# Revit family: Hand Dryer_Metlam_ABS
name_source: partatom
category: Specialty Equipment
revit_build: Autodesk Revit 2016 (Build: 20170117_1200(x64)
units: mm (PartAtom-declared; Revit-internal decimal feet)

## family parameters
Always vertical = Yes
Cut with Voids When Loaded = No
OmniClass Number = 23.40.20.21.14
OmniClass Title = Hand and Hair Dryers
Part Type = Normal
Room Calculation Point = Yes
Round Connector Dimension = Use Diameter
Shared = No
Work Plane-Based = No

## types (1)
- 260w x 180d x 217h (ML_1800_WHT)
    Description = Auto Operation ABS Hand Dryer
    Manufacturer = Metlam
    Manufacturer_Overall Depth = 180 mm  [stored 0.590551 ft]
    Manufacturer_Overall Height = 217 mm  [stored 0.711942 ft]
    Manufacturer_Overall Width = 260 mm  [stored 0.853018 ft]
    Manufacturer_Spec Code = ML_1800_WHT
    Manufacturer_URL__Product Specific = https://www.metlam.com.au
    Material_ANZRS = z_Metlam_White
    Model = ML_1800_WHT
    Type Comments = Hand Dryers
    URL = http://www.metlam.com.au
    Voltage = 240 V

note: [stored X ft] marks values corroborated as IEEE doubles in the binary element streams (Revit-internal decimal feet)

## geometry (parser evidence)
native form markers: Sweep x3
no freeform markers — native parametric forms only
